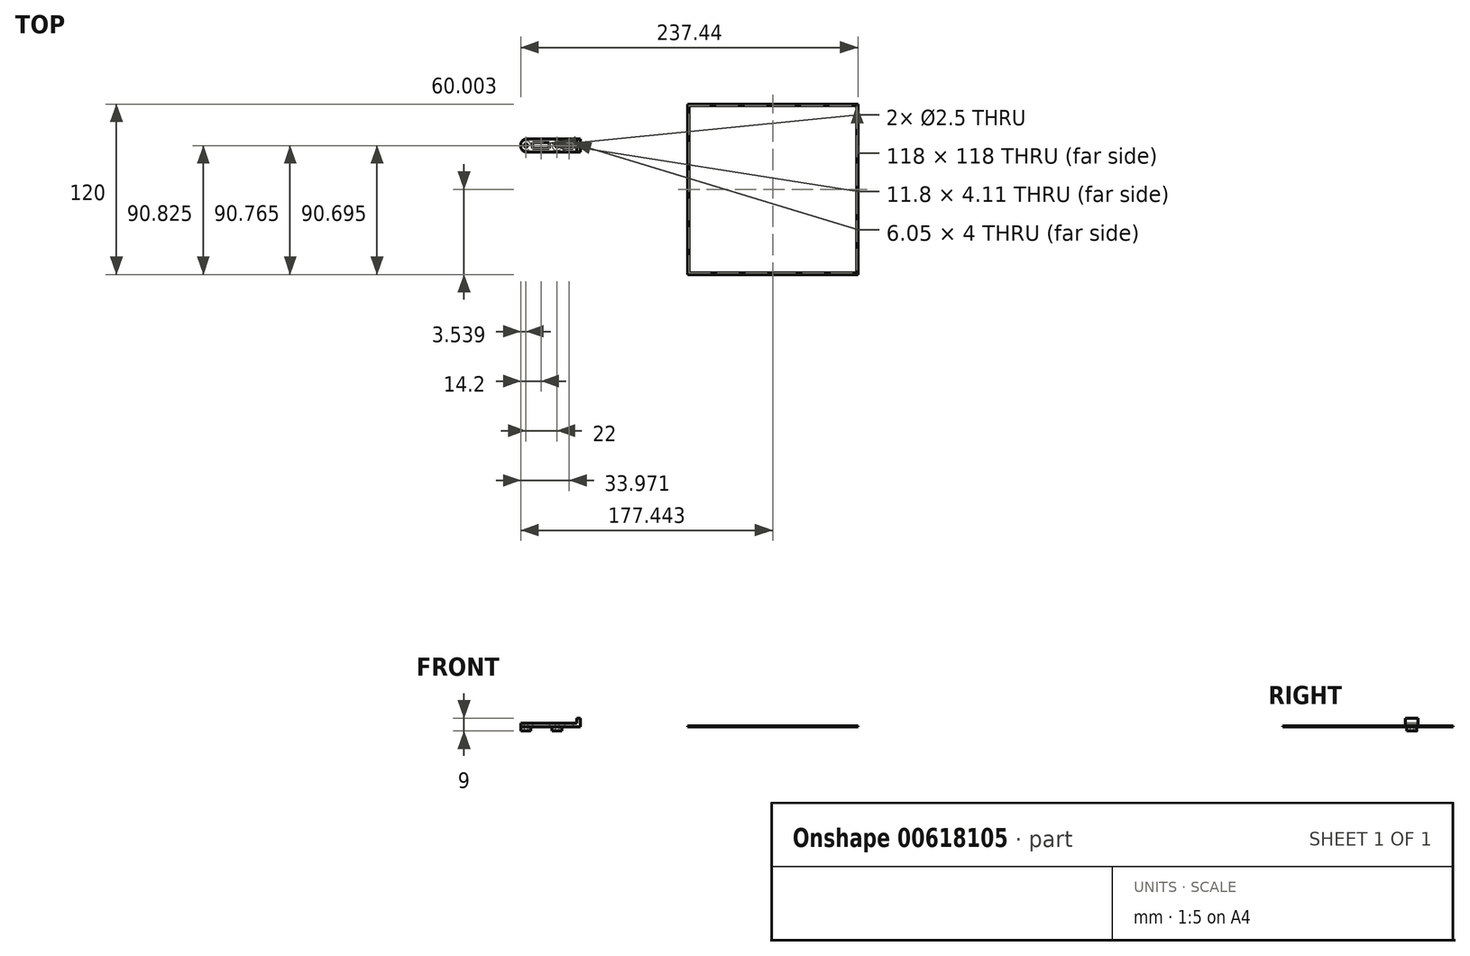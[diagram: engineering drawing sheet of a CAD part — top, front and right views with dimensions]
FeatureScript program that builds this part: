
annotation { "Feature Type Name" : "Feature", "Feature Type Description" : "" }
export const myFeature = defineFeature(function(context is Context, id is Id, definition is map)
    precondition{}
    {
        {
            var Q0;
            Q0=qCreatedBy(makeId("Top.planeOp"),FACE);
            var sketch = newSketch(context, id + "F0", { "sketchPlane" : qUnion([Q0])});
            skLineSegment(sketch, "E0.right", {"start": v(28.44, 0.98) * mm, "end": v(28.44, -8.02) * mm});
            skLineSegment(sketch, "E1.bottom", {"start": v(-7.1, 0.98) * mm, "end": v(30.99, 0.98) * mm});
            skLineSegment(sketch, "E1.top", {"start": v(-7.1, -8.02) * mm, "end": v(30.99, -8.02) * mm});
            skLineSegment(sketch, "E1.left", {"start": v(-11.1, -3.02) * mm, "end": v(-11.1, -4.02) * mm});
            skLineSegment(sketch, "E1.right", {"start": v(30.99, 0.98) * mm, "end": v(30.99, -8.02) * mm});
            skCircle(sketch, "E2", {"center": v(-7.56, -3.52) * mm, "radius": 1.25 * mm});
            skCircle(sketch, "E3", {"center": v(14.44, -3.52) * mm, "radius": 1.25 * mm});
            skPoint(sketch, "E4", {"position": v(-11.1, -3.52) * mm});
            skLineSegment(sketch, "E5", {"start": v(-11.1, -3.52) * mm, "end": v(1.25, -3.52) * mm, "construction": true});
            skPoint(sketch, "E6.visualSharp", {"position": v(-11.1, 0.98) * mm});
            skArc(sketch, "E6.filletArc", {"start": v(-7.1, 0.98) * mm, "mid": v(-9.93, -0.2) * mm, "end": v(-11.1, -3.02) * mm});
            skPoint(sketch, "E7.visualSharp", {"position": v(-11.1, -8.02) * mm});
            skArc(sketch, "E7.filletArc", {"start": v(-11.1, -4.02) * mm, "mid": v(-9.93, -6.85) * mm, "end": v(-7.1, -8.02) * mm});
            skCircle(sketch, "E8", {"center": v(-7.56, -3.52) * mm, "radius": 3.54 * mm});
            skCircle(sketch, "E9", {"center": v(14.44, -3.52) * mm, "radius": 3.54 * mm});
            skLineSegment(sketch, "E10.bottom", {"start": v(-2.8, -5.64) * mm, "end": v(9, -5.64) * mm});
            skLineSegment(sketch, "E10.top", {"start": v(-2.8, -1.53) * mm, "end": v(9, -1.53) * mm});
            skLineSegment(sketch, "E10.left", {"start": v(-2.8, -5.64) * mm, "end": v(-2.8, -1.53) * mm});
            skLineSegment(sketch, "E10.right", {"start": v(9, -5.64) * mm, "end": v(9, -1.53) * mm});
            skLineSegment(sketch, "E11.bottom", {"start": v(19.84, -5.66) * mm, "end": v(25.9, -5.66) * mm});
            skLineSegment(sketch, "E11.top", {"start": v(19.84, -1.65) * mm, "end": v(25.9, -1.65) * mm});
            skLineSegment(sketch, "E11.left", {"start": v(19.84, -5.66) * mm, "end": v(19.84, -1.65) * mm});
            skLineSegment(sketch, "E11.right", {"start": v(25.9, -5.66) * mm, "end": v(25.9, -1.65) * mm});
            skLineSegment(sketch, "E12.bottom", {"start": v(106.34, 25.65) * mm, "end": v(226.34, 25.65) * mm});
            skLineSegment(sketch, "E12.top", {"start": v(106.34, -94.35) * mm, "end": v(226.34, -94.35) * mm});
            skLineSegment(sketch, "E12.left", {"start": v(106.34, 25.65) * mm, "end": v(106.34, -94.35) * mm});
            skLineSegment(sketch, "E12.right", {"start": v(226.34, 25.65) * mm, "end": v(226.34, -94.35) * mm});
            skLineSegment(sketch, "E13.bottom", {"start": v(107.34, 24.65) * mm, "end": v(225.34, 24.65) * mm});
            skLineSegment(sketch, "E13.top", {"start": v(107.34, -93.35) * mm, "end": v(225.34, -93.35) * mm});
            skLineSegment(sketch, "E13.left", {"start": v(107.34, 24.65) * mm, "end": v(107.34, -93.35) * mm});
            skLineSegment(sketch, "E13.right", {"start": v(225.34, 24.65) * mm, "end": v(225.34, -93.35) * mm});
            skSolve(sketch);
        }
        {
            var Q0;
            Q0=makeQuery(id+"F0.imprint","IMPRINT",FACE,{"disambiguationData":[TD([[makeQuery(id+"F0.imprint","IMPRINT",EDGE,{"derivedFrom":sQuery(id+"F0.wireOp",EDGE,"E1.left")}),1.0]])]});
            var Q1;
            {var subQ5=sQuery(id+"F0.wireOp",EDGE,"E1.right");Q1=makeQuery(id+"F0.imprint","IMPRINT",FACE,{"disambiguationData":[TD([[makeQuery(id+"F0.imprint","IMPRINT",EDGE,{"derivedFrom":subQ5}),-1.0]])]});}
            var Q2;
            Q2=makeQuery(id+"F0.imprint","IMPRINT",FACE,{"disambiguationData":[TD([[makeQuery(id+"F0.imprint","IMPRINT",EDGE,{"derivedFrom":sQuery(id+"F0.wireOp",EDGE,"E2")}),-1.0]])]});
            var Q3;
            Q3=makeQuery(id+"F0.imprint","IMPRINT",FACE,{"disambiguationData":[TD([[makeQuery(id+"F0.imprint","IMPRINT",EDGE,{"derivedFrom":sQuery(id+"F0.wireOp",EDGE,"E3")}),-1.0]])]});
            extrude(context, id + "F1", {"entities" : qUnion([Q0, Q1, Q2, Q3]), "depth" : 2.5 * mm, "offsetDistance" : 25 * mm});
        }
        {
            var Q0;
            Q0=makeQuery(id+"F0.imprint","IMPRINT",FACE,{"disambiguationData":[TD([[makeQuery(id+"F0.imprint","IMPRINT",EDGE,{"derivedFrom":sQuery(id+"F0.wireOp",EDGE,"E2")}),-1.0]])]});
            var Q1;
            Q1=makeQuery(id+"F0.imprint","IMPRINT",FACE,{"disambiguationData":[TD([[makeQuery(id+"F0.imprint","IMPRINT",EDGE,{"derivedFrom":sQuery(id+"F0.wireOp",EDGE,"E3")}),-1.0]])]});
            extrude(context, id + "F2", {"entities" : qUnion([Q0, Q1]), "operationType" : NewBodyOperationType.ADD, "oppositeDirection" : true, "depth" : 3 * mm, "offsetDistance" : 25 * mm});
        }
        {
            var Q0;
            {var subQ5=sQuery(id+"F0.wireOp",EDGE,"E1.right");Q0=makeQuery(id+"F0.imprint","IMPRINT",FACE,{"disambiguationData":[TD([[makeQuery(id+"F0.imprint","IMPRINT",EDGE,{"derivedFrom":subQ5}),-1.0]])]});}
            extrude(context, id + "F3", {"entities" : qUnion([Q0]), "operationType" : NewBodyOperationType.ADD, "depth" : 6 * mm, "offsetDistance" : 25 * mm});
        }
        {
            var Q0;
            Q0 = qSketchRegion(id + "F0", true);
            extrude(context, id + "F4", {"entities" : qUnion([Q0]), "operationType" : NewBodyOperationType.ADD, "depth" : 0.7 * mm, "offsetDistance" : 25 * mm});
        }
    });
